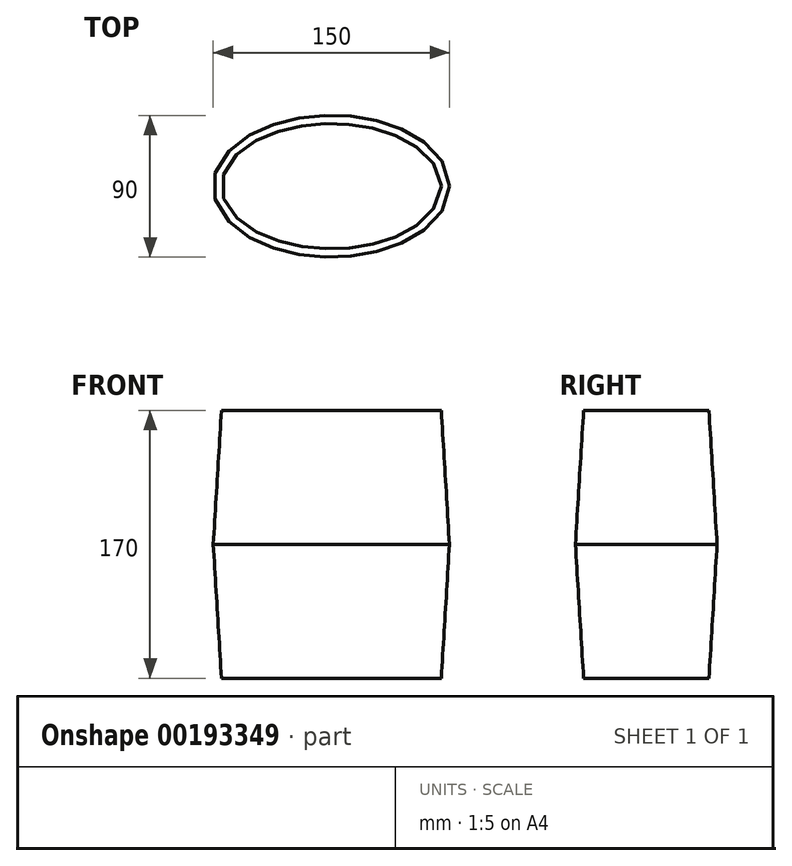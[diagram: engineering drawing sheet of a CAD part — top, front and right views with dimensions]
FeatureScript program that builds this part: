
annotation { "Feature Type Name" : "Feature", "Feature Type Description" : "" }
export const myFeature = defineFeature(function(context is Context, id is Id, definition is map)
    precondition{}
    {
        {
            var Q0;
            Q0=qCreatedBy(makeId("Top.planeOp"), FACE);
            var sketch = newSketch(context, id + "F0", { "sketchPlane" : qUnion([Q0])});
            skLineSegment(sketch, "E0", {"start": v(0, 0) * mm, "end": v(-75, 0) * mm, "construction": true});
            skLineSegment(sketch, "E1", {"start": v(0, 0) * mm, "end": v(0, 45) * mm, "construction": true});
            skLineSegment(sketch, "E2.MirrorCS", {"start": v(0, 0) * mm, "end": v(75, 0) * mm, "construction": true});
            skLineSegment(sketch, "E3.MirrorCS", {"start": v(0, 0) * mm, "end": v(0, -45) * mm, "construction": true});
            skEllipse(sketch, "E4", {"center": v(0, 0) * mm, "majorRadius": 45 * mm, "minorRadius": 75 * mm, "majorAxis": v(0, 1)});
            skSolve(sketch);
        }
        {
            var Q0;
            Q0 = qSketchRegion(id + "F0", true);
            extrude(context, id + "F1", {"entities" : qUnion([Q0]), "depth" : 85 * mm, "offsetDistance" : 25 * mm, "hasDraft" : true, "draftAngle" : 3.5 * degree, "draftPullDirection" : true, "hasSecondDirection" : true, "secondDirectionOppositeDirection" : true, "secondDirectionDepth" : 85 * mm, "hasSecondDirectionDraft" : true, "secondDirectionDraftAngle" : 3.5 * degree, "secondDirectionDraftPullDirection" : true});
        }
    });
